# Revit family: Innovo NL_IR 32 380 NL NAT
name_source: partatom
category: Mechanical Equipment
revit_build: Autodesk Revit 2015 (Build: 20160512_0715(x64)
units: mm (PartAtom-declared; Revit-internal decimal feet)

## types (1)
- IR-32-380 NL NAT
    1e Onderhoud (check-up) = 3 maanden na installatie
    2e Onderhoud (algeheel onderhoud) = 12 maanden na installatie
    Aansluiting Aftapkraan = 3/4"
    Aansluiting Condensafvoer = 40 mm  [stored 0.131234 ft]
    Aansluiting Koud Water = 3/4"
    Aansluiting T&P = 1"
    Aansluiting Warm Water = 1"
    Ander capaciteitsprofiel = 3XL
    Assembly Code = D3010
    BIM Content Developer = CAD & Company
    Bestemming / Land = Nederland
    Breedte = 675 mm  [stored 2.21457 ft]
    CE-PIN = 0063CQ3037
    CO2-uitstoot (tol. +/- 1.0) vol% = 9.3
    Capaciteitsprofiel = XXL
    Description = Condenserende Hoog Rendementsboiler
    Diameter = 675 mm  [stored 2.21457 ft]
    Diameter Schoorsteen - boiler = 80/125 mm/mm
    Diameter Schoorsteen - concentrisch systeem = 80/125 mm/mm
    Diameter Schoorsteen - parallel systeem = 2x80
    Elektrisch Vermogen (nominaal) = 85 W
    Elektrisch Vermogen (piek) = 105 W
    Energie-efficiëntie voor waterverwarming (1) = 90%
    Energie-efficiëntie voor waterverwarming (2) = 92%
    Energie-efficiëntieklasse voor waterverwarming (1) = A
    Energie-efficiëntieklasse voor waterverwarming (2) = -
    Fabrikantnummer = E 7110
    Fase = 1
    Frequentie = 50 Hz
    Garrantie op Onderdelen = 12 maanden
    Garrantie op Tank = 36 maanden
    Gas Aansluiting = 15"
    Gas Voordruk = 5000.0 Pa
    Gascategorie = II2EK3B/P
    Gasverbruik - Massa kg/h = n.v.t.
    Gasverbruik - Volume ltr/hr = 3.10
    Geluidsniveau binnen = 58 dB
    Geluidsniveau dB (A) = <45
    Handelsmerk = A.O. Smith
    Hoogte = 1745 mm
    Hoogte Gas Aansluiting = 905 mm
    Hoogte Koud Water Inlaat = 170 mm  [stored 0.557743 ft]
    Hoogte Lucht Inlaat = 1350 mm
    Hoogte Rookgasafvoer = 1350 mm
    Hoogte Warm Water Uitlaat = 1745 mm
    Inhoud = 380.0 L
    Installatie Typen = B23/C13/C33/C43/C53/C63
    Isolatiedikte = 44 mm  [stored 0.144357 ft]
    Jaarlijks brandstofverbruik (1) = 21 GJ GCV
    Jaarlijks brandstofverbruik (2) = 40 GJ GCV
    Jaarlijks elektriciteitsverbruik (1) = 45 kWh
    Jaarlijks elektriciteitsverbruik (2) = 92 kWh
    Kraan Hoogte 01 = 693 mm  [stored 2.27362 ft]
    Kraan Hoogte 02 = 1518 mm  [stored 4.98031 ft]
    Ledig Gewicht = 155 kg
    Length = 780 mm  [stored 2.55906 ft]
    Manufacturer = A.O. Smith Water Products Company b.v.
    Max. Rookgastemperatuur = 65 °C
    Max. Stand Regelthermostaat = 85 °C
    Max. Werkdruk = 800000.0 Pa
    Min. Stand Regelthermostaat = 40 °C
    Model = IR-32-380 NL NAT
    NOx-uitstoot (lucht vrij, 0% O2) ppm = 24
    NOx-uitstoot mg/kWh = 37.0
    Nominaal Vermogen = 31300.0
    Nominale Belasting (Bovenwaarde) = 32200.0
    Nominale Belasting (Onderwaarde) = 29000.0
    Onderhoudsinterval = 12 maanden
    Opwarmtijd bij ΔT = 28°C = 20
    Opwarmtijd bij ΔT = 44°C = 31
    Opwarmtijd bij ΔT = 50°C = 36
    Opwarmtijd bij ΔT = 55°C = 39
    Opwarmtijd bij ΔT = 70°C = 50
    Produkt Model Nummer (EAN-nummer) = 8717449283865
    Rendement (Hi, vlgs. NEN-EN 89 - 1999) = 108
    Rendement (Hs, vlgs. NEN-EN 89 - 1999) = 97
    Seizoens Rendement (Hs) = 97
    Setpoint thermostaat = 65 °C
    Slimme controlefunctie = No
    Soort Verpakking = Karton en Hout
    Stand Regelthermostaat = 65 °C
    Standaard Afgesteld op = G25.3
    Stilstandsverlies = 0 W
    Stilstandsverlies - dagelijks (24u) = 0 W
    Tapcapaciteit Continu bij ΔT = 28°C = 960.0 L/s
    Tapcapaciteit Continu bij ΔT = 44°C = 600.0 L/s
    Tapcapaciteit Continu bij ΔT = 50°C = 530.0 L/s
    Tapcapaciteit Continu bij ΔT = 55°C = 480.0 L/s
    Tapcapaciteit Continu bij ΔT = 70°C = 380.0 L/s
    Tapcapaciteit bij ΔT = 28°C na 120 min. = 2800.0 L
    Tapcapaciteit bij ΔT = 28°C na 30 min. = 1300.0 L
    Tapcapaciteit bij ΔT = 28°C na 60 min. = 1800.0 L
    Tapcapaciteit bij ΔT = 28°C na 90 min. = 2300.0 L
    Tapcapaciteit bij ΔT = 44°C  na 30 min. = 1800.0 L
    Tapcapaciteit bij ΔT = 44°C  na 60 min. = 790.0 L
    Tapcapaciteit bij ΔT = 44°C  na 90 min. = 1100.0 L
    Tapcapaciteit bij ΔT = 44°C na 120 min. = 1400.0 L
    Tapcapaciteit bij ΔT = 50°C  na 30 min. = 680.0 L
    Tapcapaciteit bij ΔT = 50°C  na 60 min. = 950.0 L
    Tapcapaciteit bij ΔT = 50°C  na 90 min. = 1300.0 L
    Tapcapaciteit bij ΔT = 50°C na 120 min. = 1500.0 L
    Tapcapaciteit bij ΔT = 55°C  na 120 min. = 1400.0 L
    Tapcapaciteit bij ΔT = 55°C  na 30 min. = 610.0 L
    Tapcapaciteit bij ΔT = 55°C  na 60 min. = 860.0 L
    Tapcapaciteit bij ΔT = 55°C  na 90 min. = 1100.0 L
    Tapcapaciteit bij ΔT = 70°C  na 120 min. = 1100.0 L
    Tapcapaciteit bij ΔT = 70°C  na 30 min. = 460.0 L
    Tapcapaciteit bij ΔT = 70°C  na 60 min. = 650.0 L
    Tapcapaciteit bij ΔT = 70°C  na 90 min. = 840.0 L
    Totaal Gewicht = 552 kg
    Transportgewicht = 172 kg
    Type aanduiding = IR-32-380
    URL = www.aosmith.nl
    Uitschakeldruk LDS < = 210.0 Pa
    Uitsluitend werkend in daluren = No
    Verpakkingsbreedte = 786 mm
    Verpakkingshoogte = 1895 mm
    Verpakkingslengte = 946 mm
    Voltage = 230 V
    Voorzorgsmaatregelen tijdens montage, installatie of onderhoud = zie Gebruikers, Installatie, Service en Onderhouds handleiding
    Werkruimte Afstand Voor = 1000 mm  [stored 3.28084 ft]
    Werkruimte Hoogte = 2745 mm  [stored 9.00591 ft]
    Werkruimte Radius = 845 mm

note: [stored X ft] marks values corroborated as IEEE doubles in the binary element streams (Revit-internal decimal feet)

## geometry (parser evidence)
native form markers: Blend x26, Sweep x24
no freeform markers — native parametric forms only
